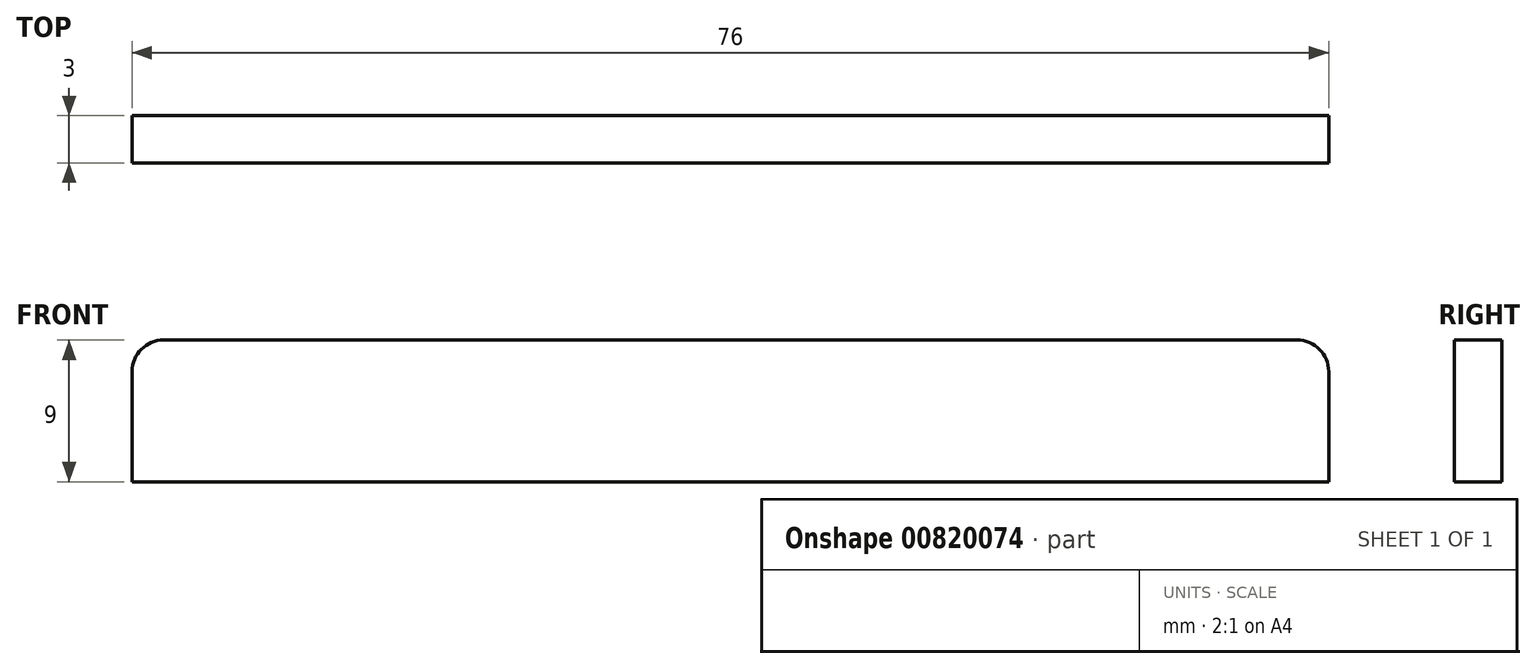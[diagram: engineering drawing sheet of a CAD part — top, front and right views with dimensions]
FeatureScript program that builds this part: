
annotation { "Feature Type Name" : "Feature", "Feature Type Description" : "" }
export const myFeature = defineFeature(function(context is Context, id is Id, definition is map)
    precondition{}
    {
        {
            var Q0;
            Q0=qCreatedBy(makeId("Top.planeOp"),FACE);
            var sketch = newSketch(context, id + "F0", { "sketchPlane" : qUnion([Q0])});
            skLineSegment(sketch, "E0.bottom", {"start": v(38, 1.5) * mm, "end": v(-38, 1.5) * mm});
            skLineSegment(sketch, "E0.top", {"start": v(38, -1.5) * mm, "end": v(-38, -1.5) * mm});
            skLineSegment(sketch, "E0.left", {"start": v(38, 1.5) * mm, "end": v(38, -1.5) * mm});
            skLineSegment(sketch, "E0.right", {"start": v(-38, 1.5) * mm, "end": v(-38, -1.5) * mm});
            skPoint(sketch, "E0.middle", {"position": v(0, 0) * mm});
            skSolve(sketch);
        }
        {
            var Q0;
            Q0=makeQuery(id+"F0.imprint","IMPRINT",FACE,{"disambiguationData":[TD([[makeQuery(id+"F0.imprint","IMPRINT",EDGE,{"derivedFrom":sQuery(id+"F0.wireOp",EDGE,"E0.bottom")}),1.0]])]});
            extrude(context, id + "F1", {"entities" : qUnion([Q0]), "depth" : 9 * mm, "offsetDistance" : 25 * mm});
        }
        {
            var Q0;
            Q0=makeQuery(id+"F1.opExtrude","CAP_EDGE",EDGE,{"disambiguationData":[OSD([sQuery(id+"F0.wireOp",EDGE,"E0.left")])],"isStart":false});
            var Q1;
            Q1=makeQuery(id+"F1.opExtrude","CAP_EDGE",EDGE,{"disambiguationData":[OSD([sQuery(id+"F0.wireOp",EDGE,"E0.right")])],"isStart":false});
            fillet(context, id + "F2", {"entities" : qUnion([Q0, Q1]), "radius" : 2 * mm, "tangentPropagation" : true, "allowEdgeOverflow" : false});
        }
    });
